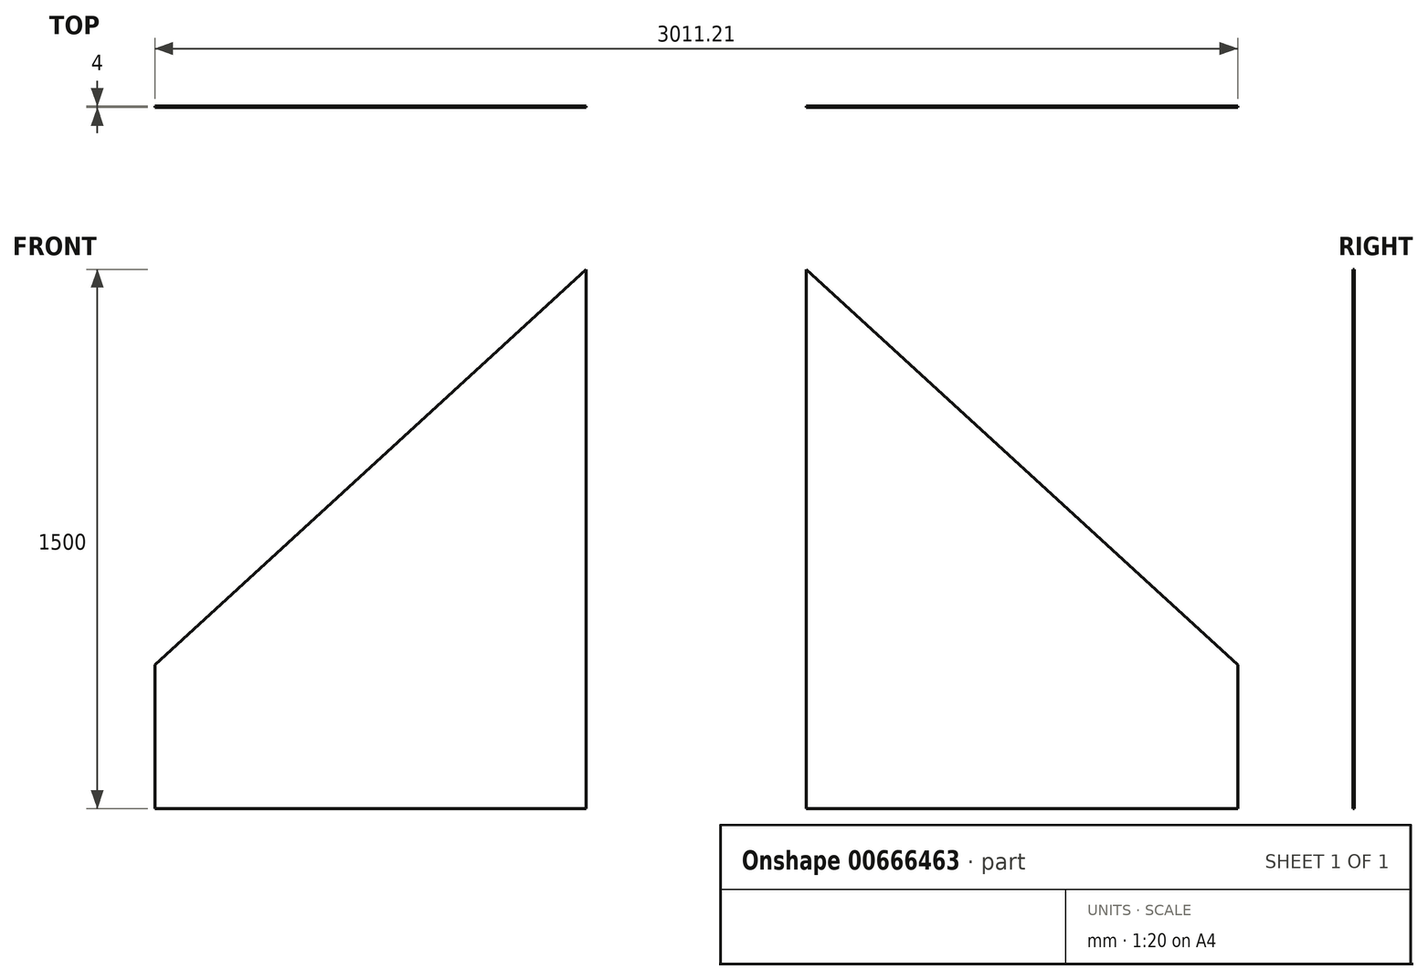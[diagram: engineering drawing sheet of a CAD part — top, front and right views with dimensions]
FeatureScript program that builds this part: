
annotation { "Feature Type Name" : "Feature", "Feature Type Description" : "" }
export const myFeature = defineFeature(function(context is Context, id is Id, definition is map)
    precondition{}
    {
        {
            var Q0;
            Q0=qCreatedBy(makeId("Front.planeOp"),FACE);
            var sketch = newSketch(context, id + "F0", { "sketchPlane" : qUnion([Q0])});
            skLineSegment(sketch, "E0", {"start": v(-1200, 0) * mm, "end": v(-1200, 400) * mm});
            skLineSegment(sketch, "E1", {"start": v(-1200, 400) * mm, "end": v(0, 1500) * mm});
            skLineSegment(sketch, "E2", {"start": v(0, 1500) * mm, "end": v(0, 0) * mm});
            skLineSegment(sketch, "E3", {"start": v(0, 0) * mm, "end": v(-1200, 0) * mm});
            skLineSegment(sketch, "E4", {"start": v(305.6, 1590.42) * mm, "end": v(305.6, -220.97) * mm, "construction": true});
            skLineSegment(sketch, "E5.MirrorCS", {"start": v(1811.21, 400) * mm, "end": v(611.21, 1500) * mm});
            skLineSegment(sketch, "E6.MirrorCS", {"start": v(611.21, 1500) * mm, "end": v(611.21, 0) * mm});
            skLineSegment(sketch, "E7.MirrorCS", {"start": v(611.21, 0) * mm, "end": v(1811.21, 0) * mm});
            skLineSegment(sketch, "E8.MirrorCS", {"start": v(1811.21, 0) * mm, "end": v(1811.21, 400) * mm});
            skSolve(sketch);
        }
        {
            var Q0;
            Q0 = qSketchRegion(id + "F0", true);
            extrude(context, id + "F1", {"entities" : qUnion([Q0]), "depth" : 4 * mm, "offsetDistance" : 25 * mm});
        }
    });
